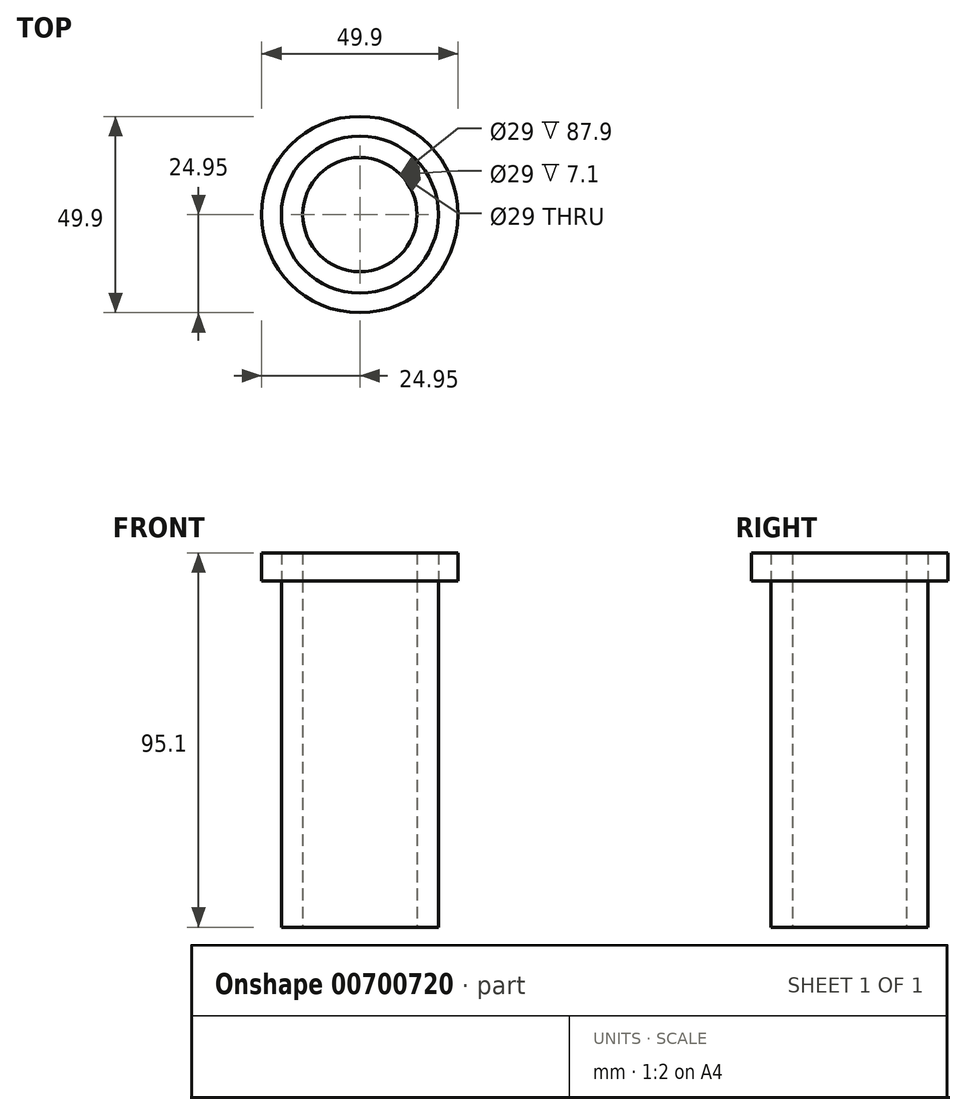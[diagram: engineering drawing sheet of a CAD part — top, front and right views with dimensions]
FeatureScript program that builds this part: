
annotation { "Feature Type Name" : "Feature", "Feature Type Description" : "" }
export const myFeature = defineFeature(function(context is Context, id is Id, definition is map)
    precondition{}
    {
        {
            var Q0;
            Q0=qCreatedBy(makeId("Top.planeOp"),FACE);
            var sketch = newSketch(context, id + "F0", { "sketchPlane" : qUnion([Q0])});
            skCircle(sketch, "E0", {"center": v(0, 0) * mm, "radius": 24.95 * mm});
            skSolve(sketch);
        }
        {
            var Q0;
            Q0 = qSketchRegion(id + "F0", true);
            extrude(context, id + "F1", {"entities" : qUnion([Q0]), "depth" : 95 * mm, "offsetDistance" : 25 * mm});
        }
        {
            var Q0;
            Q0=qCreatedBy(makeId("Top.planeOp"),FACE);
            var sketch = newSketch(context, id + "F2", { "sketchPlane" : qUnion([Q0])});
            skCircle(sketch, "E1", {"center": v(0, 0) * mm, "radius": 19.95 * mm});
            skSolve(sketch);
        }
        {
            var Q0;
            Q0 = qSketchRegion(id + "F2", true);
            extrude(context, id + "F3", {"entities" : qUnion([Q0]), "depth" : 95 * mm, "offsetDistance" : 25 * mm});
        }
        {
            var Q0;
            Q0=makeQuery(id+"F1.opExtrude","CAP_FACE",FACE,{"disambiguationData":[OSD([sQuery(id+"F0.wireOp",EDGE,"E0")])],"isStart":true});
            extrude(context, id + "F4", {"entities" : qUnion([Q0]), "operationType" : NewBodyOperationType.REMOVE, "oppositeDirection" : true, "depth" : 87.9 * mm, "offsetDistance" : 25 * mm});
        }
        {
            var Q0;
            Q0=makeQuery(id+"F4.boolean.opBoolean","COPY",FACE,{"disambiguationData":[TD([makeQuery(id+"F3.opExtrude","SWEPT_FACE",FACE,{"disambiguationData":[OSD([sQuery(id+"F2.wireOp",EDGE,"E1")])]})])],"derivedFrom":makeQuery(id+"F4.opExtrude","CAP_FACE",FACE,{"disambiguationData":[OSD([sQuery(id+"F0.wireOp",EDGE,"E0")])],"isStart":false})});
            extrude(context, id + "F5", {"entities" : qUnion([Q0]), "depth" : 88 * mm, "offsetDistance" : 25 * mm});
        }
        {
            var Q0;
            Q0=qCreatedBy(makeId("Top.planeOp"),FACE);
            var sketch = newSketch(context, id + "F6", { "sketchPlane" : qUnion([Q0])});
            skCircle(sketch, "E2", {"center": v(0, 0) * mm, "radius": 15 * mm});
            skSolve(sketch);
        }
        {
            var Q0;
            Q0=sQuery(id+"F6.wireOp",VERTEX,"E2.center");
            var Q1;
            Q1=makeQuery(id+"F1.opExtrude","SWEPT_BODY",BODY,{"disambiguationData":[OSD([sQuery(id+"F0.wireOp",EDGE,"E0")])]});
            var Q2;
            Q2=makeQuery(id+"F3.opExtrude","SWEPT_BODY",BODY,{"disambiguationData":[OSD([sQuery(id+"F2.wireOp",EDGE,"E1")])]});
            var Q3;
            Q3=makeQuery(id+"F5.opExtrude","SWEPT_BODY",BODY,{"disambiguationData":[OSD([sQuery(id+"F0.wireOp",EDGE,"E0")])]});
            hole(context, id + "F7", {"style" : HoleStyle.SIMPLE, "endStyle" : HoleEndStyle.THROUGH, "oppositeDirection" : true, "holeDiameter" : 29 * mm, "majorDiameter" : 5 * mm, "isTappedThrough" : true, "tappedDepth" : 12 * mm, "tapClearance" : 3, "locations" : qUnion([Q0]), "scope" : qUnion([Q1, Q2, Q3])});
        }
    });
